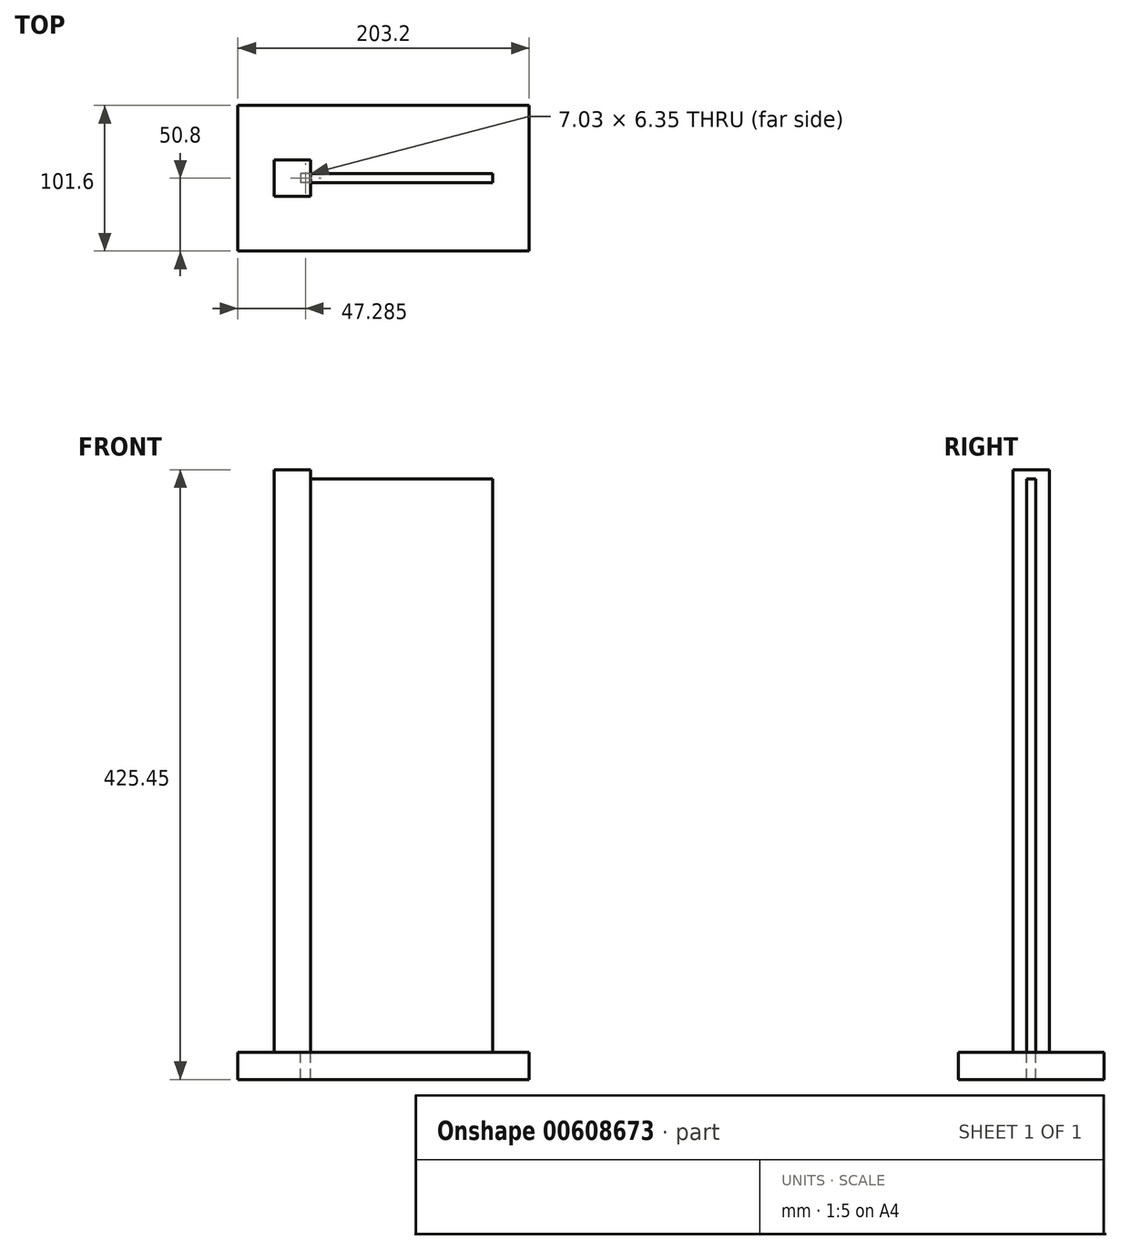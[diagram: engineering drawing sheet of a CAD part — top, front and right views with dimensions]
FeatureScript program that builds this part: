
annotation { "Feature Type Name" : "Feature", "Feature Type Description" : "" }
export const myFeature = defineFeature(function(context is Context, id is Id, definition is map)
    precondition{}
    {
        {
            var Q0;
            Q0=qCreatedBy(makeId("Top.planeOp"),FACE);
            var sketch = newSketch(context, id + "F0", { "sketchPlane" : qUnion([Q0])});
            skLineSegment(sketch, "E0.bottom", {"start": v(-101.6, 50.8) * mm, "end": v(101.6, 50.8) * mm});
            skLineSegment(sketch, "E0.top", {"start": v(-101.6, -50.8) * mm, "end": v(101.6, -50.8) * mm});
            skLineSegment(sketch, "E0.left", {"start": v(-101.6, 50.8) * mm, "end": v(-101.6, -50.8) * mm});
            skLineSegment(sketch, "E0.right", {"start": v(101.6, 50.8) * mm, "end": v(101.6, -50.8) * mm});
            skPoint(sketch, "E0.middle", {"position": v(0, 0) * mm});
            skLineSegment(sketch, "E1.bottom", {"start": v(-50.8, 12.7) * mm, "end": v(-76.2, 12.7) * mm});
            skLineSegment(sketch, "E1.top", {"start": v(-50.8, -12.7) * mm, "end": v(-76.2, -12.7) * mm});
            skLineSegment(sketch, "E1.left", {"start": v(-50.8, 12.7) * mm, "end": v(-50.8, -12.7) * mm});
            skLineSegment(sketch, "E1.right", {"start": v(-76.2, 12.7) * mm, "end": v(-76.2, -12.7) * mm});
            skPoint(sketch, "E1.middle", {"position": v(-63.5, 0) * mm});
            skLineSegment(sketch, "E2.bottom", {"start": v(-50.8, 3.18) * mm, "end": v(76.2, 3.18) * mm});
            skLineSegment(sketch, "E2.top", {"start": v(-50.8, -3.18) * mm, "end": v(76.2, -3.18) * mm});
            skLineSegment(sketch, "E2.left", {"start": v(-50.8, 3.18) * mm, "end": v(-50.8, -3.18) * mm});
            skLineSegment(sketch, "E2.right", {"start": v(76.2, 3.18) * mm, "end": v(76.2, -3.17) * mm});
            skPoint(sketch, "E2.middle", {"position": v(12.7, 0) * mm});
            skLineSegment(sketch, "E3.bottom", {"start": v(-50.8, 3.18) * mm, "end": v(-57.83, 3.18) * mm});
            skLineSegment(sketch, "E3.top", {"start": v(-50.8, -3.17) * mm, "end": v(-57.83, -3.18) * mm});
            skLineSegment(sketch, "E3.right", {"start": v(-57.83, 3.18) * mm, "end": v(-57.83, -3.18) * mm});
            skSolve(sketch);
        }
        {
            var Q0;
            Q0=makeQuery(id+"F0.imprint","IMPRINT",FACE,{"disambiguationData":[TD([[makeQuery(id+"F0.imprint","IMPRINT",EDGE,{"derivedFrom":sQuery(id+"F0.wireOp",EDGE,"E0.bottom")}),-1.0]])]});
            var Q1;
            {var subQ3=sQuery(id+"F0.wireOp",EDGE,"E1.bottom");Q1=makeQuery(id+"F0.imprint","IMPRINT",FACE,{"disambiguationData":[TD([[makeQuery(id+"F0.imprint","IMPRINT",EDGE,{"derivedFrom":subQ3}),1.0]])]});}
            var Q2;
            Q2=makeQuery(id+"F0.imprint","IMPRINT",FACE,{"disambiguationData":[TD([[makeQuery(id+"F0.imprint","IMPRINT",EDGE,{"derivedFrom":sQuery(id+"F0.wireOp",EDGE,"E2.bottom")}),-1.0]])]});
            extrude(context, id + "F1", {"entities" : qUnion([Q0, Q1, Q2]), "oppositeDirection" : true, "depth" : 19.05 * mm, "offsetDistance" : 25.4 * mm});
        }
        {
            var Q0;
            {var subQ3=sQuery(id+"F0.wireOp",EDGE,"E1.bottom");Q0=makeQuery(id+"F0.imprint","IMPRINT",FACE,{"disambiguationData":[TD([[makeQuery(id+"F0.imprint","IMPRINT",EDGE,{"derivedFrom":subQ3}),1.0]])]});}
            extrude(context, id + "F2", {"entities" : qUnion([Q0]), "depth" : 406.4 * mm, "offsetDistance" : 25.4 * mm});
        }
        {
            var Q0;
            Q0=makeQuery(id+"F0.imprint","IMPRINT",FACE,{"disambiguationData":[TD([[makeQuery(id+"F0.imprint","IMPRINT",EDGE,{"derivedFrom":sQuery(id+"F0.wireOp",EDGE,"E2.bottom")}),-1.0]])]});
            var Q1;
            Q1=makeQuery(id+"F0.imprint","IMPRINT",FACE,{"disambiguationData":[TD([[makeQuery(id+"F0.imprint","IMPRINT",EDGE,{"derivedFrom":sQuery(id+"F0.wireOp",EDGE,"E3.bottom")}),1.0]])]});
            extrude(context, id + "F3", {"entities" : qUnion([Q0, Q1]), "depth" : 400.05 * mm, "offsetDistance" : 25.4 * mm});
        }
        {
            var Q0;
            Q0=makeQuery(id+"F2.opExtrude","CAP_FACE",FACE,{"disambiguationData":[OSD([sQuery(id+"F0.wireOp",EDGE,"E1.bottom"),sQuery(id+"F0.wireOp",EDGE,"E1.top"),sQuery(id+"F0.wireOp",EDGE,"E1.left"),sQuery(id+"F0.wireOp",EDGE,"E1.right"),sQuery(id+"F0.wireOp",EDGE,"E3.bottom"),sQuery(id+"F0.wireOp",EDGE,"E3.top"),sQuery(id+"F0.wireOp",EDGE,"E3.right")])],"isStart":false});
            var sketch = newSketch(context, id + "F4", { "sketchPlane" : qUnion([Q0])});
            skLineSegment(sketch, "E4.0.0", {"start": v(-57.83, 3.18) * mm, "end": v(-50.8, 3.18) * mm});
            skLineSegment(sketch, "E4.0.1", {"start": v(-50.8, 3.18) * mm, "end": v(-50.8, 12.7) * mm});
            skLineSegment(sketch, "E4.0.2", {"start": v(-50.8, 12.7) * mm, "end": v(-76.2, 12.7) * mm});
            skLineSegment(sketch, "E4.0.3", {"start": v(-76.2, 12.7) * mm, "end": v(-76.2, -12.7) * mm});
            skLineSegment(sketch, "E4.0.4", {"start": v(-76.2, -12.7) * mm, "end": v(-50.8, -12.7) * mm});
            skLineSegment(sketch, "E4.0.5", {"start": v(-50.8, -12.7) * mm, "end": v(-50.8, -3.18) * mm});
            skLineSegment(sketch, "E4.0.6", {"start": v(-50.8, -3.17) * mm, "end": v(-57.83, -3.18) * mm});
            skLineSegment(sketch, "E4.0.7", {"start": v(-57.83, -3.18) * mm, "end": v(-57.83, 3.18) * mm});
            skLineSegment(sketch, "E5", {"start": v(-50.8, 3.18) * mm, "end": v(-50.8, -3.18) * mm});
            skSolve(sketch);
        }
        {
            var Q0;
            Q0=makeQuery(id+"F4.imprint","IMPRINT",FACE,{"disambiguationData":[TD([[makeQuery(id+"F4.imprint","IMPRINT",EDGE,{"derivedFrom":sQuery(id+"F4.wireOp",EDGE,"E4.0.0")}),-1.0]])]});
            var Q1;
            Q1=makeQuery(id+"F4.imprint","IMPRINT",FACE,{"disambiguationData":[TD([[makeQuery(id+"F4.imprint","IMPRINT",EDGE,{"derivedFrom":sQuery(id+"F4.wireOp",EDGE,"E4.0.0")}),1.0]])]});
            extrude(context, id + "F5", {"entities" : qUnion([Q0, Q1]), "operationType" : NewBodyOperationType.ADD, "oppositeDirection" : true, "depth" : 6.35 * mm, "offsetDistance" : 25.4 * mm});
        }
    });
